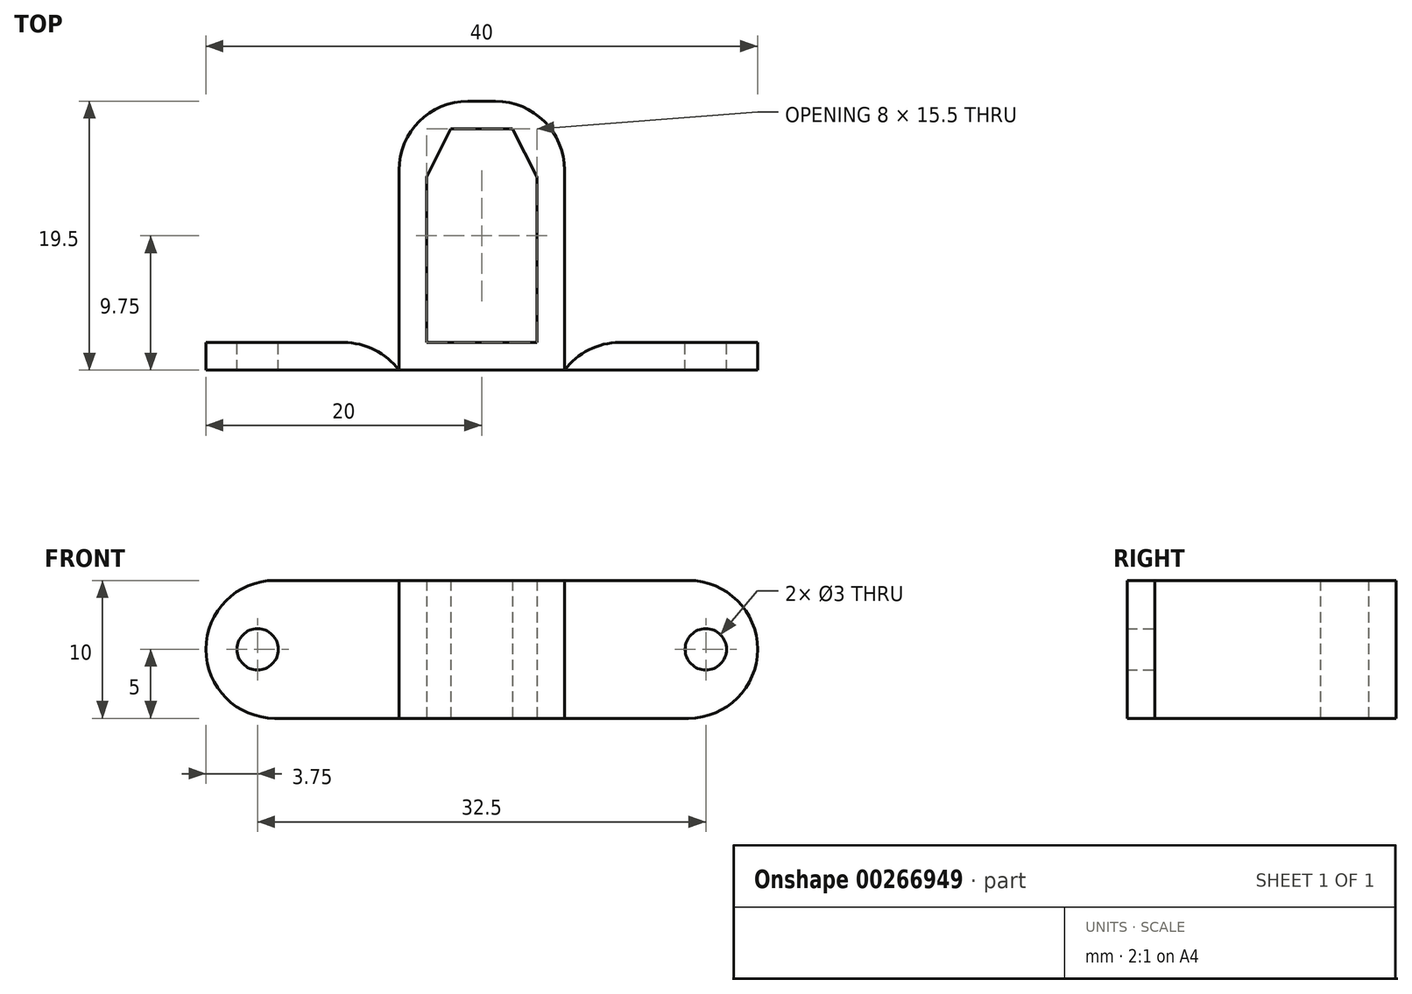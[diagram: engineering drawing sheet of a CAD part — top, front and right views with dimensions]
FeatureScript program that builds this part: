
annotation { "Feature Type Name" : "Feature", "Feature Type Description" : "" }
export const myFeature = defineFeature(function(context is Context, id is Id, definition is map)
    precondition{}
    {
        {
            var Q0;
            Q0=qCreatedBy(makeId("Top.planeOp"),FACE);
            var sketch = newSketch(context, id + "F0", { "sketchPlane" : qUnion([Q0])});
            skLineSegment(sketch, "E0", {"start": v(0, 0) * mm, "end": v(-4, 0) * mm});
            skLineSegment(sketch, "E1", {"start": v(-4, 0) * mm, "end": v(-4, 12) * mm});
            skLineSegment(sketch, "E2", {"start": v(-4, 12) * mm, "end": v(-2.23, 15.5) * mm});
            skLineSegment(sketch, "E3", {"start": v(-2.23, 15.5) * mm, "end": v(2.23, 15.5) * mm});
            skLineSegment(sketch, "E4", {"start": v(2.23, 15.5) * mm, "end": v(4, 12) * mm});
            skLineSegment(sketch, "E5", {"start": v(4, 12) * mm, "end": v(4, 0) * mm});
            skLineSegment(sketch, "E6", {"start": v(4, 0) * mm, "end": v(0, 0) * mm});
            skLineSegment(sketch, "E7.bottom", {"start": v(6, 0) * mm, "end": v(-6, 0) * mm});
            skLineSegment(sketch, "E7.top", {"start": v(6, 17.5) * mm, "end": v(-6, 17.5) * mm});
            skLineSegment(sketch, "E7.left", {"start": v(6, 0) * mm, "end": v(6, 17.5) * mm});
            skLineSegment(sketch, "E7.right", {"start": v(-6, 0) * mm, "end": v(-6, 17.5) * mm});
            skPoint(sketch, "E8", {"position": v(0, 17.5) * mm});
            skLineSegment(sketch, "E9", {"start": v(-6, 0) * mm, "end": v(-6, -2) * mm});
            skLineSegment(sketch, "E10", {"start": v(-6, -2) * mm, "end": v(6, -2) * mm});
            skLineSegment(sketch, "E11", {"start": v(6, -2) * mm, "end": v(6, 0) * mm});
            skSolve(sketch);
        }
        {
            var Q0;
            Q0 = qSketchRegion(id + "F0", true);
            extrude(context, id + "F1", {"entities" : qUnion([Q0]), "depth" : 10 * mm});
        }
        {
            var Q0;
            Q0=makeQuery(id+"F1.opExtrude","CAP_FACE",FACE,{"disambiguationData":[OSD([sQuery(id+"F0.wireOp",EDGE,"E1"),sQuery(id+"F0.wireOp",EDGE,"E2"),sQuery(id+"F0.wireOp",EDGE,"E3"),sQuery(id+"F0.wireOp",EDGE,"E4"),sQuery(id+"F0.wireOp",EDGE,"E5"),sQuery(id+"F0.wireOp",EDGE,"E7.bottom"),sQuery(id+"F0.wireOp",EDGE,"E7.top"),sQuery(id+"F0.wireOp",EDGE,"E7.left"),sQuery(id+"F0.wireOp",EDGE,"E7.right"),sQuery(id+"F0.wireOp",EDGE,"E9"),sQuery(id+"F0.wireOp",EDGE,"E10"),sQuery(id+"F0.wireOp",EDGE,"E11")])],"isStart":false});
            var sketch = newSketch(context, id + "F2", { "sketchPlane" : qUnion([Q0])});
            skLineSegment(sketch, "E12", {"start": v(-6, 0) * mm, "end": v(-20, 0) * mm});
            skLineSegment(sketch, "E13", {"start": v(-20, 0) * mm, "end": v(-20, -2) * mm});
            skLineSegment(sketch, "E14", {"start": v(-20, -2) * mm, "end": v(-6, -2) * mm});
            skLineSegment(sketch, "E15", {"start": v(-6, -2) * mm, "end": v(6, -2) * mm});
            skLineSegment(sketch, "E16", {"start": v(6, -2) * mm, "end": v(20, -2) * mm});
            skLineSegment(sketch, "E17", {"start": v(20, -2) * mm, "end": v(20, 0) * mm});
            skLineSegment(sketch, "E18", {"start": v(20, 0) * mm, "end": v(6, 0) * mm});
            skLineSegment(sketch, "E19", {"start": v(6, 0) * mm, "end": v(0, 0) * mm});
            skLineSegment(sketch, "E20", {"start": v(0, 0) * mm, "end": v(-6, 0) * mm});
            skSolve(sketch);
        }
        {
            var Q0;
            {var subQ0=sQuery(id+"F2.wireOp",EDGE,"E12");Q0=makeQuery(id+"F2.imprint","IMPRINT",FACE,{"disambiguationData":[TD([[makeQuery(id+"F2.imprint","IMPRINT",EDGE,{"derivedFrom":subQ0}),1.0]])]});}
            var Q1;
            {var subQ0=sQuery(id+"F2.wireOp",EDGE,"E16");Q1=makeQuery(id+"F2.imprint","IMPRINT",FACE,{"disambiguationData":[TD([[makeQuery(id+"F2.imprint","IMPRINT",EDGE,{"derivedFrom":subQ0}),1.0]])]});}
            extrude(context, id + "F3", {"entities" : qUnion([Q0, Q1]), "oppositeDirection" : true, "depth" : 10 * mm});
        }
        {
            var Q0;
            Q0=makeQuery(id+"F3.opExtrude","SWEPT_FACE",FACE,{"disambiguationData":[OSD([sQuery(id+"F2.wireOp",EDGE,"E12")])]});
            var sketch = newSketch(context, id + "F4", { "sketchPlane" : qUnion([Q0])});
            skCircle(sketch, "E21", {"center": v(16.25, 5) * mm, "radius": 1.5 * mm});
            skCircle(sketch, "E22.MirrorC", {"center": v(-16.25, 5) * mm, "radius": 1.5 * mm});
            skSolve(sketch);
        }
        {
            var Q0;
            Q0 = qSketchRegion(id + "F4", true);
            extrude(context, id + "F5", {"entities" : qUnion([Q0]), "operationType" : NewBodyOperationType.REMOVE, "oppositeDirection" : true, "depth" : 25 * mm});
        }
        {
            var Q0;
            Q0=makeQuery(id+"F1.opExtrude","SWEPT_EDGE",EDGE,{"disambiguationData":[OSD([sQuery(id+"F0.wireOp",EDGE,"E7.top"),sQuery(id+"F0.wireOp",EDGE,"E7.right")])]});
            var Q1;
            Q1=makeQuery(id+"F1.opExtrude","SWEPT_EDGE",EDGE,{"disambiguationData":[OSD([sQuery(id+"F0.wireOp",EDGE,"E7.top"),sQuery(id+"F0.wireOp",EDGE,"E7.left")])]});
            var Q2;
            Q2=makeQuery(id+"F3.opExtrude","SWEPT_EDGE",EDGE,{"disambiguationData":[OSD([sQuery(id+"F0.wireOp",EDGE,"E7.right"),sQuery(id+"F0.wireOp",EDGE,"E9"),sQuery(id+"F2.wireOp",EDGE,"E12"),sQuery(id+"F2.wireOp",EDGE,"E20")])]});
            var Q3;
            Q3=makeQuery(id+"F3.opExtrude","SWEPT_EDGE",EDGE,{"disambiguationData":[OSD([sQuery(id+"F0.wireOp",EDGE,"E7.left"),sQuery(id+"F0.wireOp",EDGE,"E11"),sQuery(id+"F2.wireOp",EDGE,"E18"),sQuery(id+"F2.wireOp",EDGE,"E19")])]});
            var Q4;
            Q4=makeQuery(id+"F3.opExtrude","CAP_EDGE",EDGE,{"disambiguationData":[OSD([sQuery(id+"F2.wireOp",EDGE,"E13")])],"isStart":true});
            var Q5;
            Q5=makeQuery(id+"F3.opExtrude","CAP_EDGE",EDGE,{"disambiguationData":[OSD([sQuery(id+"F2.wireOp",EDGE,"E13")])],"isStart":false});
            var Q6;
            Q6=makeQuery(id+"F3.opExtrude","CAP_EDGE",EDGE,{"disambiguationData":[OSD([sQuery(id+"F2.wireOp",EDGE,"E17")])],"isStart":true});
            var Q7;
            Q7=makeQuery(id+"F3.opExtrude","CAP_EDGE",EDGE,{"disambiguationData":[OSD([sQuery(id+"F2.wireOp",EDGE,"E17")])],"isStart":false});
            fillet(context, id + "F6", {"entities" : qUnion([Q0, Q1, Q2, Q3, Q4, Q5, Q6, Q7]), "radius" : 5 * mm, "tangentPropagation" : true, "allowEdgeOverflow" : false});
        }
    });
